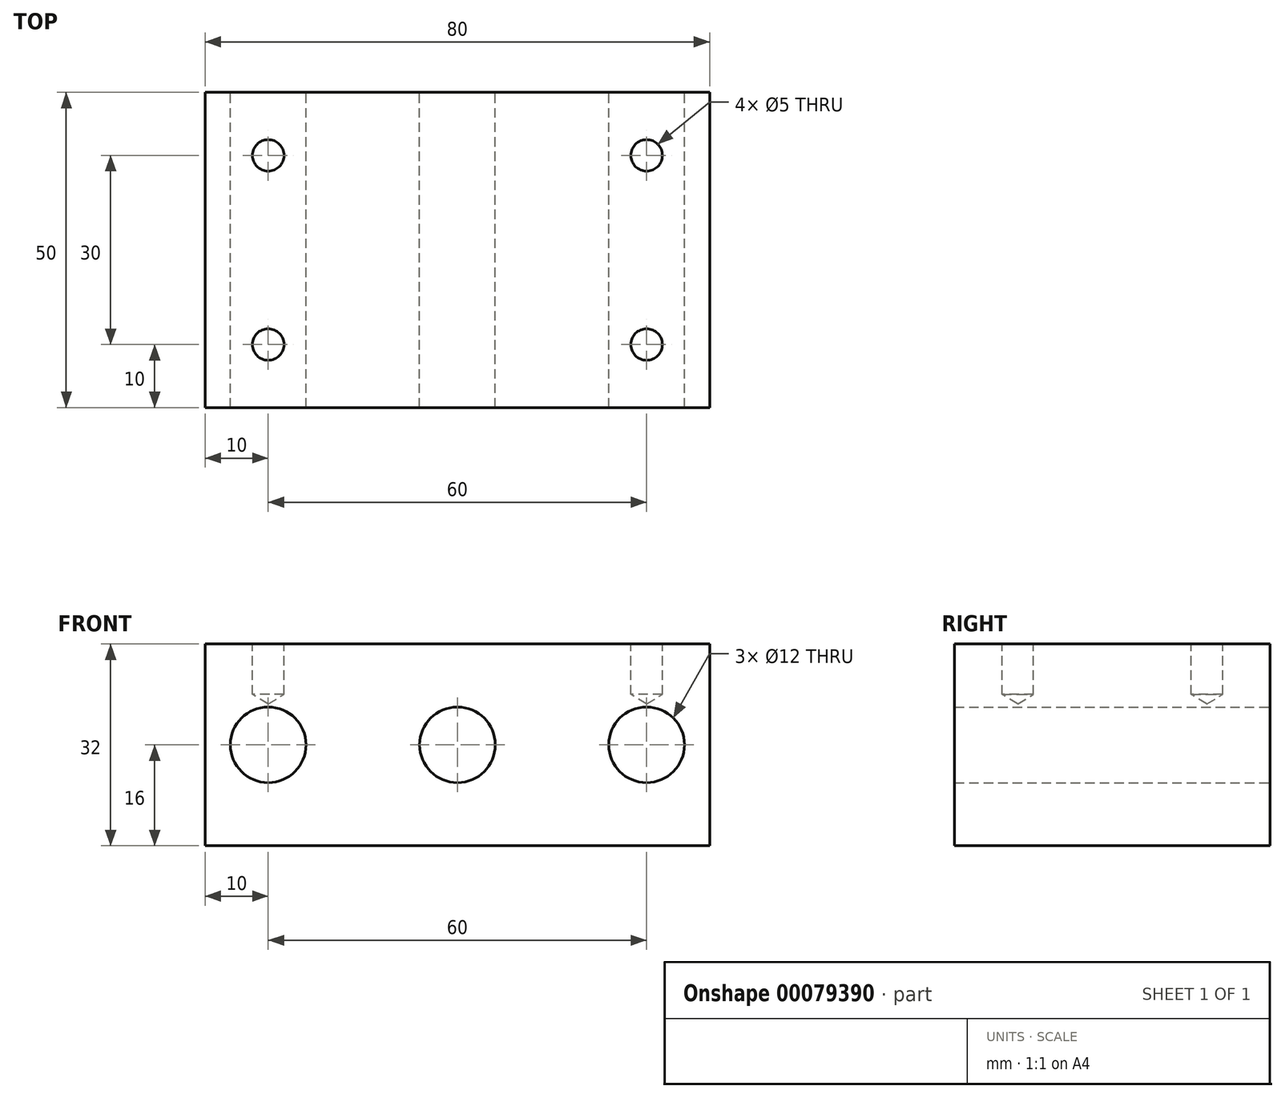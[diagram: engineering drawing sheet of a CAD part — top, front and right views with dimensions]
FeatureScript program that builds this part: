
annotation { "Feature Type Name" : "Feature", "Feature Type Description" : "" }
export const myFeature = defineFeature(function(context is Context, id is Id, definition is map)
    precondition{}
    {
        {
            var Q0;
            Q0=qCreatedBy(makeId("Front.planeOp"),FACE);
            var sketch = newSketch(context, id + "F0", { "sketchPlane" : qUnion([Q0])});
            skLineSegment(sketch, "E0.bottom", {"start": v(-40, 16) * mm, "end": v(40, 16) * mm});
            skLineSegment(sketch, "E0.top", {"start": v(-40, -16) * mm, "end": v(40, -16) * mm});
            skLineSegment(sketch, "E0.left", {"start": v(-40, 16) * mm, "end": v(-40, -16) * mm});
            skLineSegment(sketch, "E0.right", {"start": v(40, 16) * mm, "end": v(40, -16) * mm});
            skPoint(sketch, "E0.middle", {"position": v(0, 0) * mm});
            skCircle(sketch, "E1", {"center": v(0, 0) * mm, "radius": 6 * mm});
            skCircle(sketch, "E2.1.0.0", {"center": v(30, 0) * mm, "radius": 6 * mm});
            skCircle(sketch, "E3", {"center": v(-30, 0) * mm, "radius": 6 * mm});
            skSolve(sketch);
        }
        {
            var Q0;
            Q0=makeQuery(id+"F0.imprint","IMPRINT",FACE,{"disambiguationData":[TD([[makeQuery(id+"F0.imprint","IMPRINT",EDGE,{"derivedFrom":sQuery(id+"F0.wireOp",EDGE,"E0.bottom")}),-1.0]])]});
            extrude(context, id + "F1", {"entities" : qUnion([Q0]), "depth" : 50 * mm});
        }
        {
            var Q0;
            Q0=makeQuery(id+"F1.opExtrude","SWEPT_FACE",FACE,{"disambiguationData":[OSD([sQuery(id+"F0.wireOp",EDGE,"E0.bottom")])]});
            var sketch = newSketch(context, id + "F2", { "sketchPlane" : qUnion([Q0])});
            skLineSegment(sketch, "E4.bottom", {"start": v(-40, 0) * mm, "end": v(40, 0) * mm});
            skLineSegment(sketch, "E4.top", {"start": v(-40, -50) * mm, "end": v(40, -50) * mm});
            skLineSegment(sketch, "E4.left", {"start": v(-40, 0) * mm, "end": v(-40, -50) * mm});
            skLineSegment(sketch, "E4.right", {"start": v(40, 0) * mm, "end": v(40, -50) * mm});
            skPoint(sketch, "E5.middle", {"position": v(0, -25) * mm});
            skCircle(sketch, "E6", {"center": v(-30, -40) * mm, "radius": 3 * mm});
            skCircle(sketch, "E7", {"center": v(-30, -10) * mm, "radius": 3 * mm});
            skCircle(sketch, "E8", {"center": v(30, -40) * mm, "radius": 3 * mm});
            skCircle(sketch, "E9", {"center": v(30, -10) * mm, "radius": 3 * mm});
            skPoint(sketch, "E10.endSnap0", {"position": v(0, -50) * mm});
            skPoint(sketch, "E10.end.orphan", {"position": v(0, 12.95) * mm});
            skSolve(sketch);
        }
        {
            var Q0;
            Q0=sQuery(id+"F2.wireOp",VERTEX,"E6.center");
            var Q1;
            Q1=sQuery(id+"F2.wireOp",VERTEX,"E7.center");
            var Q2;
            Q2=sQuery(id+"F2.wireOp",VERTEX,"E8.center");
            var Q3;
            Q3=sQuery(id+"F2.wireOp",VERTEX,"E9.center");
            var Q4;
            Q4=makeQuery(id+"F1.opExtrude","SWEPT_BODY",BODY,{"disambiguationData":[OSD([sQuery(id+"F0.wireOp",EDGE,"E0.bottom"),sQuery(id+"F0.wireOp",EDGE,"E0.top"),sQuery(id+"F0.wireOp",EDGE,"E0.left"),sQuery(id+"F0.wireOp",EDGE,"E0.right"),sQuery(id+"F0.wireOp",EDGE,"E1"),sQuery(id+"F0.wireOp",EDGE,"E2.1.0.0"),sQuery(id+"F0.wireOp",EDGE,"E3")])]});
            hole(context, id + "F3", {"style" : HoleStyle.SIMPLE, "endStyle" : HoleEndStyle.BLIND, "holeDiameter" : 5 * mm, "holeDepth" : 8 * mm, "locations" : qUnion([Q0, Q1, Q2, Q3]), "scope" : qUnion([Q4])});
        }
    });
